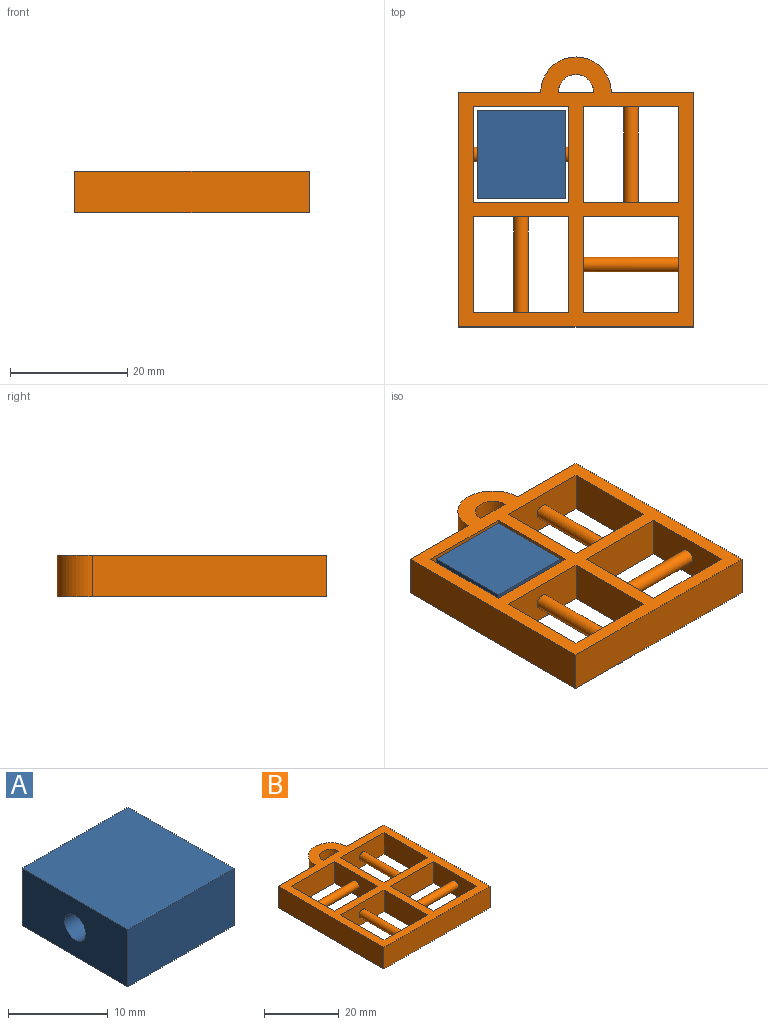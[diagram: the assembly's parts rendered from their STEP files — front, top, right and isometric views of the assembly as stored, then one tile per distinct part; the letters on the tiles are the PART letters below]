
ASSEMBLY  parts=2 mates=1
PART A: 31 faces, bbox 15x15x7 mm
  f0: plane 15x15mm, normal (0,0,-1), area 188.6mm2, adj f1,f2,f3,f4,f7,f8,f9,f10
  f1: plane 15x7mm, normal (0,1,0), area 105mm2, adj f0,f2,f4,f5
  f2: plane 15x7mm, normal (-1,0,0), area 97.9mm2, adj f0,f1,f3,f5,f6
  f3: plane 15x7mm, normal (0,-1,0), area 105mm2, adj f0,f2,f4,f5
  f4: plane 15x7mm, normal (1,0,0), area 97.9mm2, adj f0,f1,f3,f5,f6
  f5: plane 15x15mm, normal (0,0,1), area 225mm2, adj f1,f2,f3,f4
  f6: cylinder r=1.5mm len=15mm, axis (1,0,0), area 141.4mm2, adj f2,f4
  f7: plane 1.5x1.28mm, normal (1,0,0), area 1.9mm2, adj f0,f8,f29,f30
  f8: plane 6.67x1.5mm, normal (0,-1,0), area 10mm2, adj f0,f7,f9,f30
  f9: plane 2.47x1.5mm, normal (-1,0,0), area 3.7mm2, adj f0,f8,f10,f30
  f10: plane 1.5x1.49mm, normal (0,1,0), area 2.2mm2, adj f0,f9,f11,f30
  f11: plane 1.5x0.97mm, normal (1,0.08,0), area 1.5mm2, adj f0,f10,f12,f30
  f12: plane 2.54x1.5mm, normal (0,1,0), area 3.8mm2, adj f0,f11,f13,f30
  f13: plane 1.5x0.03mm, normal (-0.94,0.35,0), area 0.1mm2, adj f0,f12,f14,f30
  f14: plane 1.9x1.74mm, normal (-0.74,-0.68,0), area 3.9mm2, adj f0,f13,f15,f30
  f15: extruded ~1.96x1.61mm, area 3.8mm2, adj f0,f14,f16,f30
  f16: extruded ~1.64x1.5mm, area 2.6mm2, adj f0,f15,f17,f30
  f17: extruded ~2.09x1.5mm, area 3.5mm2, adj f0,f16,f18,f30
  f18: extruded ~2.37x1.5mm, area 3.8mm2, adj f0,f17,f19,f30
  f19: extruded ~2.43x1.5mm, area 4mm2, adj f0,f18,f20,f30
  f20: extruded ~2.24x1.5mm, area 3.7mm2, adj f0,f19,f21,f30
  f21: plane 1.5x0.04mm, normal (0.94,-0.35,0), area 0.1mm2, adj f0,f20,f22,f30
  f22: plane 1.9x1.5mm, normal (0,-1,0), area 2.9mm2, adj f0,f21,f23,f30
  f23: extruded ~1.5x1.23mm, area 1.9mm2, adj f0,f22,f24,f30
  f24: extruded ~1.5x1.03mm, area 1.8mm2, adj f0,f23,f25,f30
  f25: extruded ~1.5x0.94mm, area 1.6mm2, adj f0,f24,f26,f30
  f26: extruded ~1.5x1.01mm, area 1.6mm2, adj f0,f25,f27,f30
  f27: extruded ~1.5x1mm, area 1.6mm2, adj f0,f26,f28,f30
  f28: extruded ~1.5x1.33mm, area 2.5mm2, adj f0,f27,f29,f30
  f29: plane 3.39x3.16mm, normal (0.73,0.68,0), area 7mm2, adj f0,f7,f28,f30
  f30: plane 9.91x6.86mm, normal (0,0,-1), area 36.4mm2, adj f7,f8,f9,f10,f11,f12,f13,f14
PART B: 30 faces, bbox 40x46x7 mm
  f0: plane 14x7mm, normal (0,1,0), area 98mm2, adj f21,f22,f23,f28
  f1: plane 7x6mm, normal (0,1,0), area 42mm2, adj f22,f23,f29
  f2: plane 14x7mm, normal (0,1,0), area 98mm2, adj f3,f22,f23,f28
  f3: plane 40x7mm, normal (-1,0,0), area 280mm2, adj f2,f4,f22,f23
  f4: plane 40x7mm, normal (0,-1,0), area 280mm2, adj f3,f21,f22,f23
  f5: plane 16.25x7mm, normal (0,1,0), area 108.8mm2, adj f6,f17,f22,f23,f25
  f6: plane 16.25x7mm, normal (1,0,0), area 113.8mm2, adj f5,f7,f22,f23
  f7: plane 16.25x7mm, normal (0,-1,0), area 108.8mm2, adj f6,f17,f22,f23,f25
  f8: plane 16.25x7mm, normal (1,0,0), area 108.8mm2, adj f9,f18,f22,f23,f27
  f9: plane 16.25x7mm, normal (0,-1,0), area 113.8mm2, adj f8,f10,f22,f23
  f10: plane 16.25x7mm, normal (-1,0,0), area 108.8mm2, adj f9,f18,f22,f23,f27
  f11: plane 16.25x7mm, normal (0,-1,0), area 108.8mm2, adj f12,f19,f22,f23,f26
  f12: plane 16.25x7mm, normal (-1,0,0), area 113.8mm2, adj f11,f13,f22,f23
  f13: plane 16.25x7mm, normal (0,1,0), area 108.8mm2, adj f12,f19,f22,f23,f26
  f14: plane 16.25x7mm, normal (1,0,0), area 108.8mm2, adj f15,f20,f22,f23,f24
  f15: plane 16.25x7mm, normal (0,-1,0), area 113.8mm2, adj f14,f16,f22,f23
  f16: plane 16.25x7mm, normal (-1,0,0), area 108.8mm2, adj f15,f20,f22,f23,f24
  f17: plane 16.25x7mm, normal (-1,0,0), area 113.8mm2, adj f5,f7,f22,f23
  f18: plane 16.25x7mm, normal (0,1,0), area 113.8mm2, adj f8,f10,f22,f23
  f19: plane 16.25x7mm, normal (1,0,0), area 113.8mm2, adj f11,f13,f22,f23
  f20: plane 16.25x7mm, normal (0,1,0), area 113.8mm2, adj f14,f16,f22,f23
  f21: plane 40x7mm, normal (1,0,0), area 280mm2, adj f0,f4,f22,f23
  f22: plane 46x40mm, normal (0,0,1), area 586.2mm2, adj f0,f1,f2,f3,f4,f5,f6,f7
  f23: plane 46x40mm, normal (0,0,-1), area 586.2mm2, adj f0,f1,f2,f3,f4,f5,f6,f7
  f24: cylinder r=1.25mm len=16.25mm, axis (-1,0,0), area 127.6mm2, adj f14,f16
  f25: cylinder r=1.25mm len=16.25mm, axis (0,-1,0), area 127.6mm2, adj f5,f7
  f26: cylinder r=1.25mm len=16.25mm, axis (0,-1,0), area 127.6mm2, adj f11,f13
  f27: cylinder r=1.25mm len=16.25mm, axis (1,0,0), area 127.6mm2, adj f8,f10
  f28: cylinder r=6mm len=12mm, axis (0,0,1), area 131.9mm2, adj f0,f2,f22,f23
  f29: cylinder r=3mm len=7mm, axis (0,0,1), area 66mm2, adj f1,f22,f23
PLACE A t=(9.23,-4.63,4.69)mm
PLACE B t=(18.51,-14.01,4.69)mm
MATE cylindrical A.f6 <-> B.f24  axis (1,0,0) through (1.73,-4.63,8.19)mm
